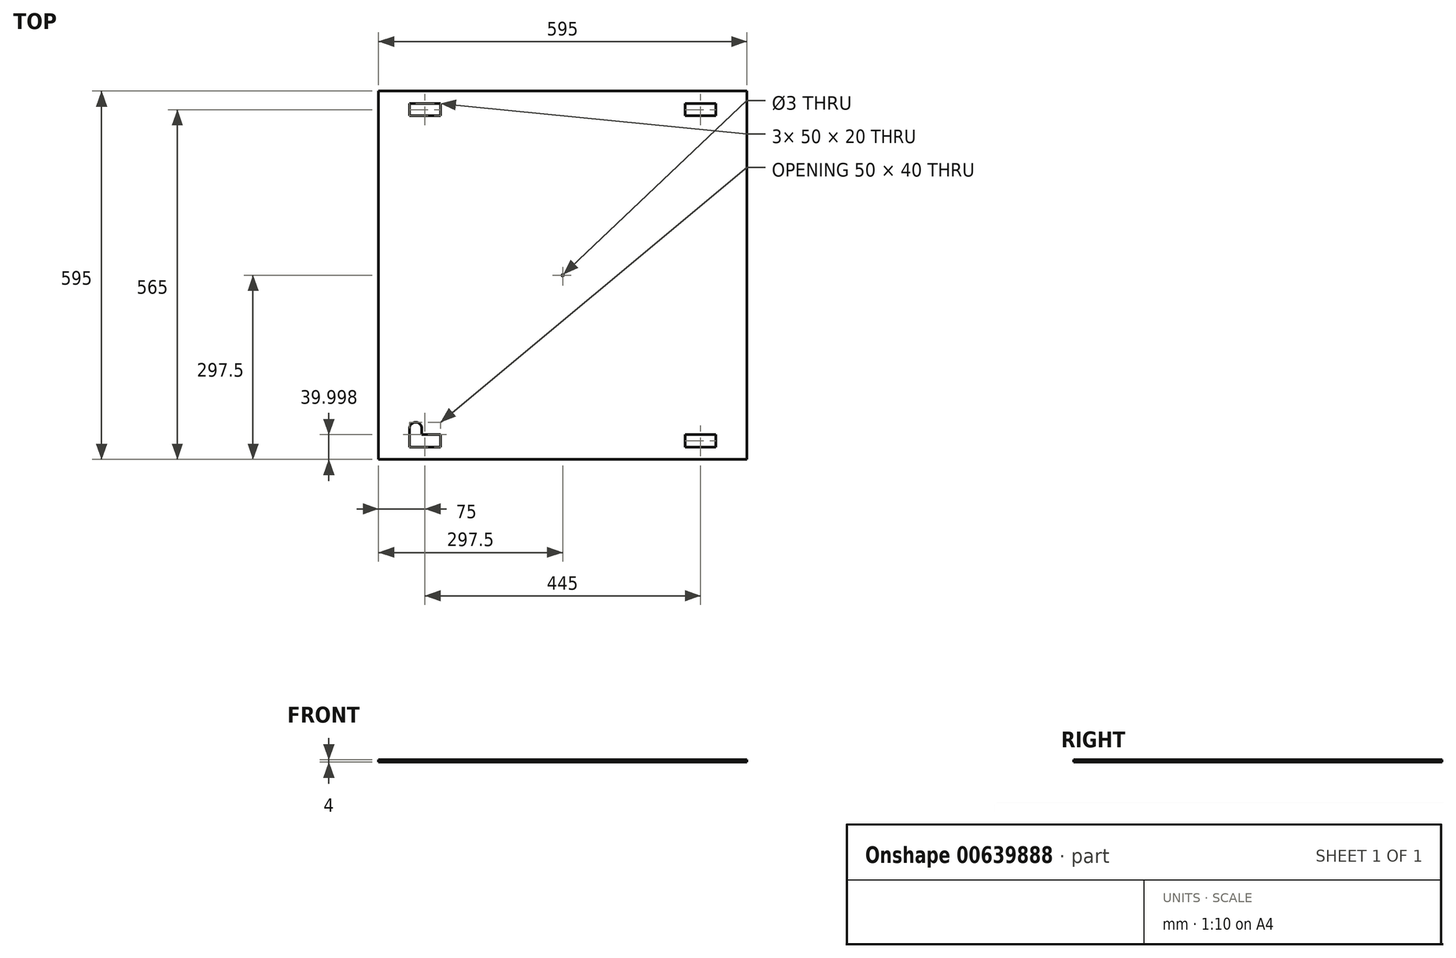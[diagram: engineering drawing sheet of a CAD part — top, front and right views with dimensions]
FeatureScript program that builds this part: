
annotation { "Feature Type Name" : "Feature", "Feature Type Description" : "" }
export const myFeature = defineFeature(function(context is Context, id is Id, definition is map)
    precondition{}
    {
        {
            var Q0;
            Q0=qCreatedBy(makeId("Top.planeOp"), FACE);
            var sketch = newSketch(context, id + "F0", { "sketchPlane" : qUnion([Q0])});
            skLineSegment(sketch, "E0.bottom", {"start": v(297.5, -297.5) * mm, "end": v(-297.5, -297.5) * mm});
            skLineSegment(sketch, "E0.top", {"start": v(297.5, 297.5) * mm, "end": v(-297.5, 297.5) * mm});
            skLineSegment(sketch, "E0.left", {"start": v(297.5, -297.5) * mm, "end": v(297.5, 297.5) * mm});
            skLineSegment(sketch, "E0.right", {"start": v(-297.5, -297.5) * mm, "end": v(-297.5, 297.5) * mm});
            skPoint(sketch, "E0.middle", {"position": v(0, 0) * mm});
            skLineSegment(sketch, "E1.bottom", {"start": v(247.5, -277.5) * mm, "end": v(-247.5, -277.5) * mm, "construction": true});
            skLineSegment(sketch, "E1.top", {"start": v(247.5, 277.5) * mm, "end": v(-247.5, 277.5) * mm, "construction": true});
            skLineSegment(sketch, "E1.left", {"start": v(247.5, -277.5) * mm, "end": v(247.5, 277.5) * mm, "construction": true});
            skLineSegment(sketch, "E1.right", {"start": v(-247.5, -277.5) * mm, "end": v(-247.5, 277.5) * mm, "construction": true});
            skLineSegment(sketch, "E2.bottom", {"start": v(197.5, 257.5) * mm, "end": v(-197.5, 257.5) * mm, "construction": true});
            skLineSegment(sketch, "E2.top", {"start": v(197.5, -257.5) * mm, "end": v(-197.5, -257.5) * mm, "construction": true});
            skLineSegment(sketch, "E2.left", {"start": v(197.5, 257.5) * mm, "end": v(197.5, -257.5) * mm, "construction": true});
            skLineSegment(sketch, "E2.right", {"start": v(-197.5, 257.5) * mm, "end": v(-197.5, -257.5) * mm, "construction": true});
            skLineSegment(sketch, "E3.bottom", {"start": v(-247.5, 277.5) * mm, "end": v(-197.5, 277.5) * mm});
            skLineSegment(sketch, "E3.top", {"start": v(-247.5, 257.5) * mm, "end": v(-197.5, 257.5) * mm});
            skLineSegment(sketch, "E3.left", {"start": v(-247.5, 277.5) * mm, "end": v(-247.5, 257.5) * mm});
            skLineSegment(sketch, "E3.right", {"start": v(-197.5, 277.5) * mm, "end": v(-197.5, 257.5) * mm});
            skLineSegment(sketch, "E4.bottom", {"start": v(197.5, 257.5) * mm, "end": v(247.5, 257.5) * mm});
            skLineSegment(sketch, "E4.top", {"start": v(197.5, 277.5) * mm, "end": v(247.5, 277.5) * mm});
            skLineSegment(sketch, "E4.left", {"start": v(197.5, 257.5) * mm, "end": v(197.5, 277.5) * mm});
            skLineSegment(sketch, "E4.right", {"start": v(247.5, 257.5) * mm, "end": v(247.5, 277.5) * mm});
            skLineSegment(sketch, "E5.bottom", {"start": v(197.5, -257.5) * mm, "end": v(247.5, -257.5) * mm});
            skLineSegment(sketch, "E5.top", {"start": v(197.5, -277.5) * mm, "end": v(247.5, -277.5) * mm});
            skLineSegment(sketch, "E5.left", {"start": v(197.5, -257.5) * mm, "end": v(197.5, -277.5) * mm});
            skLineSegment(sketch, "E5.right", {"start": v(247.5, -257.5) * mm, "end": v(247.5, -277.5) * mm});
            skLineSegment(sketch, "E6.bottom", {"start": v(-247.5, -277.5) * mm, "end": v(-197.5, -277.5) * mm});
            skLineSegment(sketch, "E6.top", {"start": v(-247.5, -257.5) * mm, "end": v(-237.5, -257.5) * mm, "construction": true});
            skLineSegment(sketch, "E6.left", {"start": v(-247.5, -277.5) * mm, "end": v(-247.5, -257.5) * mm});
            skLineSegment(sketch, "E6.right", {"start": v(-197.5, -277.5) * mm, "end": v(-197.5, -257.5) * mm});
            skCircle(sketch, "E7", {"center": v(0, 0) * mm, "radius": 1.5 * mm});
            skArc(sketch, "E8", {"start": v(-247.5, -247.5) * mm, "mid": v(-244.57, -254.57) * mm, "end": v(-237.5, -257.5) * mm, "construction": true});
            skArc(sketch, "E9", {"start": v(-237.5, -257.5) * mm, "mid": v(-230.26, -254.4) * mm, "end": v(-227.51, -247) * mm, "construction": true});
            skLineSegment(sketch, "E10", {"start": v(-237.5, -257.5) * mm, "end": v(-227.51, -257.5) * mm, "construction": true});
            skLineSegment(sketch, "E11", {"start": v(-247.5, -247.5) * mm, "end": v(-247.5, -257.5) * mm});
            skLineSegment(sketch, "E12", {"start": v(-227.51, -247) * mm, "end": v(-227.51, -257.5) * mm});
            skArc(sketch, "E13", {"start": v(-227.51, -247) * mm, "mid": v(-237.75, -237.5) * mm, "end": v(-247.5, -247.5) * mm});
            skLineSegment(sketch, "E14", {"start": v(-227.51, -257.5) * mm, "end": v(-197.5, -257.5) * mm});
            skSolve(sketch);
        }
        {
            var Q0;
            Q0 = qSketchRegion(id + "F0", true);
            extrude(context, id + "F1", {"entities" : qUnion([Q0]), "domain" : OperationDomain.MODEL, "flatOperationType" : FlatOperationType.REMOVE, "depth" : 4 * mm, "offsetDistance" : 25 * mm});
        }
    });
